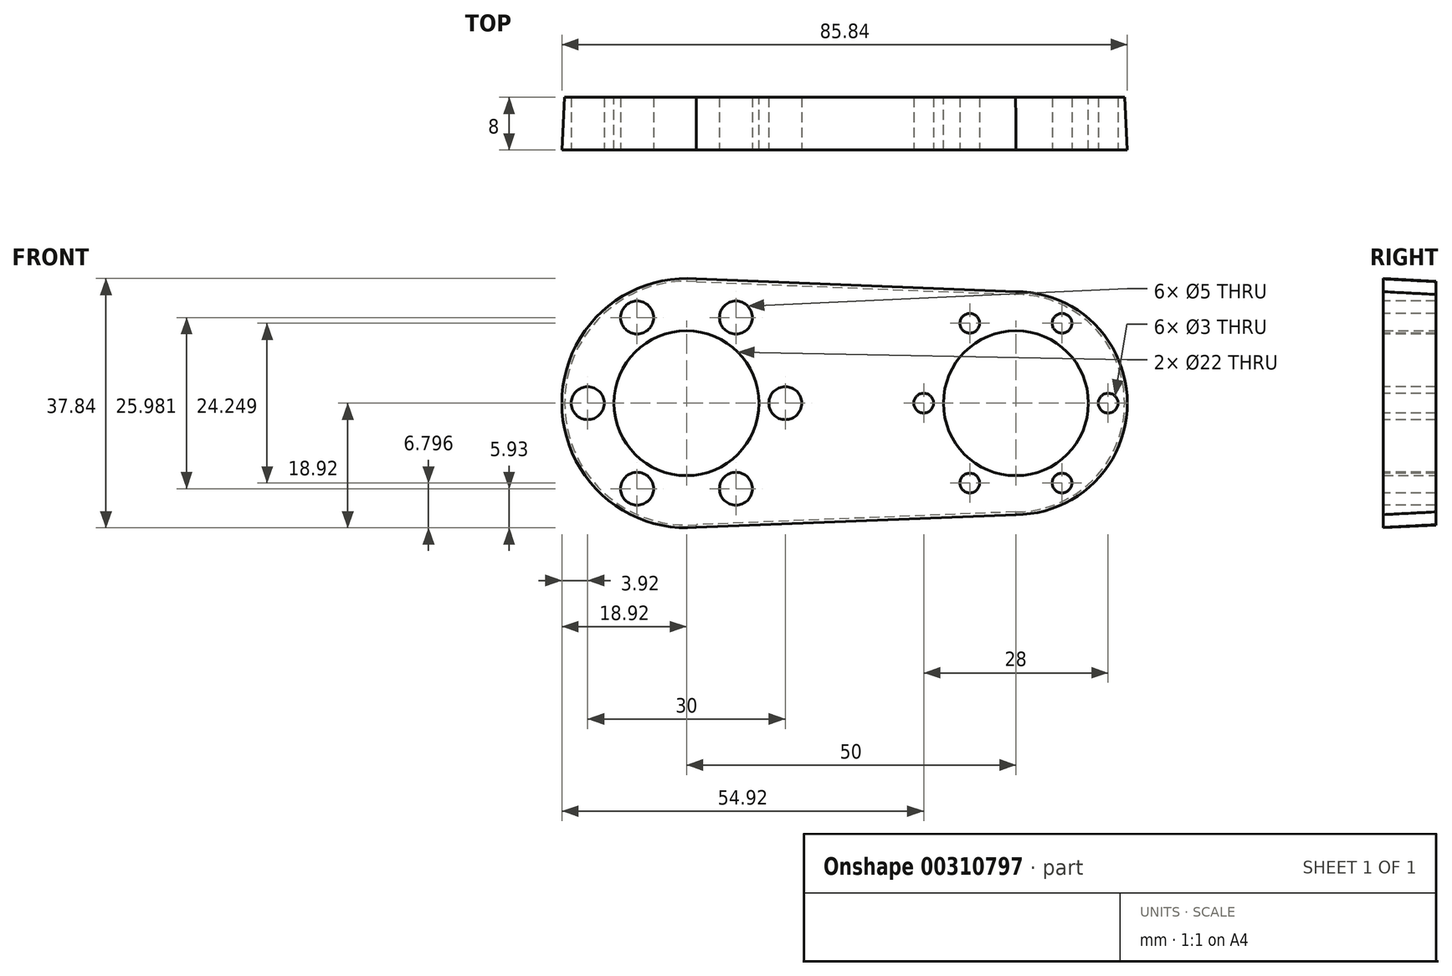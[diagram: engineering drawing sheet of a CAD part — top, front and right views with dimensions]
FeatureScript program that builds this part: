
annotation { "Feature Type Name" : "Feature", "Feature Type Description" : "" }
export const myFeature = defineFeature(function(context is Context, id is Id, definition is map)
    precondition{}
    {
        {
            var Q0;
            Q0=qCreatedBy(makeId("Front.planeOp"),FACE);
            var sketch = newSketch(context, id + "F0", { "sketchPlane" : qUnion([Q0])});
            skCircle(sketch, "E0", {"center": v(0, 0) * mm, "radius": 18.5 * mm});
            skCircle(sketch, "E1", {"center": v(50, 0) * mm, "radius": 16.5 * mm});
            skLineSegment(sketch, "E2", {"start": v(0, 0) * mm, "end": v(50, 0) * mm});
            skLineSegment(sketch, "E3.MirrorCS", {"start": v(0, -18.5) * mm, "end": v(51.35, -16.44) * mm});
            skPoint(sketch, "E4.orphan", {"position": v(0, 18.5) * mm});
            skPoint(sketch, "E5.end.orphan", {"position": v(51.35, 16.44) * mm});
            skPoint(sketch, "E6.orphan", {"position": v(0, -18.5) * mm});
            skLineSegment(sketch, "E7.MirrorCS", {"start": v(0, 18.5) * mm, "end": v(51.35, 16.44) * mm});
            skSolve(sketch);
        }
        {
            var Q0;
            Q0 = qSketchRegion(id + "F0", true);
            extrude(context, id + "F1", {"entities" : qUnion([Q0]), "depth" : 8 * mm, "hasDraft" : true, "draftAngle" : 3 * degree});
        }
        {
            var Q0;
            Q0=qCreatedBy(makeId("Front.planeOp"),FACE);
            var sketch = newSketch(context, id + "F2", { "sketchPlane" : qUnion([Q0])});
            skCircle(sketch, "E8", {"center": v(0, 0) * mm, "radius": 12.5 * mm});
            skCircle(sketch, "E9", {"center": v(50, 0) * mm, "radius": 11 * mm});
            skLineSegment(sketch, "E10", {"start": v(0, 0) * mm, "end": v(50, 0) * mm});
            skSolve(sketch);
        }
        {
            var Q0;
            Q0=sQuery(id+"F2.wireOp",VERTEX,"E9.center");
            var Q1;
            Q1=makeQuery(id+"F1.opExtrude","SWEPT_BODY",BODY,{"disambiguationData":[OSD([sQuery(id+"F0.wireOp",EDGE,"E0"),sQuery(id+"F0.wireOp",EDGE,"E1"),sQuery(id+"F0.wireOp",EDGE,"lOm7dpQ5-tVep-HTj6-Fg3J-5uafw6nHa8Ga"),sQuery(id+"F0.wireOp",EDGE,"7add0b8c-7404-4d7d-8fd4-b24f55b45dc70.MirrorCS")])]});
            hole(context, id + "F3", {"style" : HoleStyle.SIMPLE, "endStyle" : HoleEndStyle.THROUGH, "oppositeDirection" : true, "holeDiameter" : 22 * mm, "tappedDepth" : 12.7 * mm, "tapClearance" : 3, "locations" : qUnion([Q0]), "scope" : qUnion([Q1])});
        }
        {
            var Q0;
            Q0=sQuery(id+"F2.wireOp",VERTEX,"E8.center");
            var Q1;
            Q1=makeQuery(id+"F1.opExtrude","SWEPT_BODY",BODY,{"disambiguationData":[OSD([sQuery(id+"F0.wireOp",EDGE,"E0"),sQuery(id+"F0.wireOp",EDGE,"E1"),sQuery(id+"F0.wireOp",EDGE,"lOm7dpQ5-tVep-HTj6-Fg3J-5uafw6nHa8Ga"),sQuery(id+"F0.wireOp",EDGE,"7add0b8c-7404-4d7d-8fd4-b24f55b45dc70.MirrorCS")])]});
            hole(context, id + "F4", {"style" : HoleStyle.SIMPLE, "endStyle" : HoleEndStyle.THROUGH, "oppositeDirection" : true, "holeDiameter" : 22 * mm, "tappedDepth" : 12.7 * mm, "tapClearance" : 3, "locations" : qUnion([Q0]), "scope" : qUnion([Q1])});
        }
        {
            var Q0;
            Q0=makeQuery(id+"F1.opExtrude","CAP_FACE",FACE,{"disambiguationData":[OSD([sQuery(id+"F0.wireOp",EDGE,"E0"),sQuery(id+"F0.wireOp",EDGE,"E1"),sQuery(id+"F0.wireOp",EDGE,"E3.MirrorCS"),sQuery(id+"F0.wireOp",EDGE,"E7.MirrorCS")])],"isStart":false});
            var sketch = newSketch(context, id + "F5", { "sketchPlane" : qUnion([Q0])});
            skCircle(sketch, "E11", {"center": v(15, 0) * mm, "radius": 2.5 * mm});
            skCircle(sketch, "E12", {"center": v(36, 0) * mm, "radius": 1.5 * mm});
            skCircle(sketch, "E13.1.0", {"center": v(7.5, 13) * mm, "radius": 2.5 * mm});
            skCircle(sketch, "E13.2.0", {"center": v(-7.5, 13) * mm, "radius": 2.5 * mm});
            skPoint(sketch, "E13.center", {"position": v(0, 0) * mm});
            skCircle(sketch, "E14.1.3.0", {"center": v(-15, 0) * mm, "radius": 2.5 * mm});
            skCircle(sketch, "E15.1.0", {"center": v(43, -12.12) * mm, "radius": 1.5 * mm});
            skCircle(sketch, "E15.2.0", {"center": v(57, -12.12) * mm, "radius": 1.5 * mm});
            skCircle(sketch, "E15.3.0", {"center": v(64, 0) * mm, "radius": 1.5 * mm});
            skPoint(sketch, "E15.center", {"position": v(50, 0) * mm});
            skCircle(sketch, "E16.1.4.0", {"center": v(57, 12.12) * mm, "radius": 1.5 * mm});
            skCircle(sketch, "E16.1.5.0", {"center": v(43, 12.12) * mm, "radius": 1.5 * mm});
            skCircle(sketch, "E17.1.4.0", {"center": v(-7.5, -13) * mm, "radius": 2.5 * mm});
            skCircle(sketch, "E17.1.5.0", {"center": v(7.5, -13) * mm, "radius": 2.5 * mm});
            skSolve(sketch);
        }
        {
            var Q0;
            Q0=sQuery(id+"F5.wireOp",VERTEX,"E11.center");
            var Q1;
            Q1=sQuery(id+"F5.wireOp",VERTEX,"E13.1.0.center");
            var Q2;
            Q2=sQuery(id+"F5.wireOp",VERTEX,"E13.2.0.center");
            var Q3;
            Q3=sQuery(id+"F5.wireOp",VERTEX,"E14.1.3.0.center");
            var Q4;
            Q4=sQuery(id+"F5.wireOp",VERTEX,"E17.1.4.0.center");
            var Q5;
            Q5=sQuery(id+"F5.wireOp",VERTEX,"E17.1.5.0.center");
            var Q6;
            Q6=makeQuery(id+"F1.opExtrude","SWEPT_BODY",BODY,{"disambiguationData":[OSD([sQuery(id+"F0.wireOp",EDGE,"E0"),sQuery(id+"F0.wireOp",EDGE,"E1"),sQuery(id+"F0.wireOp",EDGE,"E3.MirrorCS"),sQuery(id+"F0.wireOp",EDGE,"E7.MirrorCS")])]});
            hole(context, id + "F6", {"style" : HoleStyle.SIMPLE, "endStyle" : HoleEndStyle.THROUGH, "holeDiameter" : 5 * mm, "tappedDepth" : 12.7 * mm, "tapClearance" : 3, "locations" : qUnion([Q0, Q1, Q2, Q3, Q4, Q5]), "scope" : qUnion([Q6])});
        }
        {
            var Q0;
            Q0=sQuery(id+"F5.wireOp",VERTEX,"E12.center");
            var Q1;
            Q1=sQuery(id+"F5.wireOp",VERTEX,"E16.1.5.0.center");
            var Q2;
            Q2=sQuery(id+"F5.wireOp",VERTEX,"E16.1.4.0.center");
            var Q3;
            Q3=sQuery(id+"F5.wireOp",VERTEX,"E15.3.0.center");
            var Q4;
            Q4=sQuery(id+"F5.wireOp",VERTEX,"E15.2.0.center");
            var Q5;
            Q5=sQuery(id+"F5.wireOp",VERTEX,"E15.1.0.center");
            var Q6;
            Q6=makeQuery(id+"F1.opExtrude","SWEPT_BODY",BODY,{"disambiguationData":[OSD([sQuery(id+"F0.wireOp",EDGE,"E0"),sQuery(id+"F0.wireOp",EDGE,"E1"),sQuery(id+"F0.wireOp",EDGE,"E3.MirrorCS"),sQuery(id+"F0.wireOp",EDGE,"E7.MirrorCS")])]});
            hole(context, id + "F7", {"style" : HoleStyle.SIMPLE, "endStyle" : HoleEndStyle.THROUGH, "holeDiameter" : 3 * mm, "tappedDepth" : 12.7 * mm, "tapClearance" : 3, "locations" : qUnion([Q0, Q1, Q2, Q3, Q4, Q5]), "scope" : qUnion([Q6])});
        }
        {
            var Q0;
            Q0=sQuery(id+"F5.wireOp",VERTEX,"E15.3.0.center");
            var Q1;
            Q1=sQuery(id+"F5.wireOp",VERTEX,"E15.2.0.center");
            var Q2;
            Q2=sQuery(id+"F5.wireOp",VERTEX,"E15.1.0.center");
            var Q3;
            Q3=sQuery(id+"F5.wireOp",VERTEX,"E12.center");
            var Q4;
            Q4=makeQuery(id+"F1.opExtrude","SWEPT_BODY",BODY,{"disambiguationData":[OSD([sQuery(id+"F0.wireOp",EDGE,"E0"),sQuery(id+"F0.wireOp",EDGE,"E1"),sQuery(id+"F0.wireOp",EDGE,"E3.MirrorCS"),sQuery(id+"F0.wireOp",EDGE,"E7.MirrorCS")])]});
            hole(context, id + "F8", {"style" : HoleStyle.SIMPLE, "endStyle" : HoleEndStyle.THROUGH, "holeDiameter" : 3 * mm, "tappedDepth" : 12.7 * mm, "tapClearance" : 3, "locations" : qUnion([Q0, Q1, Q2, Q3]), "scope" : qUnion([Q4])});
        }
    });
